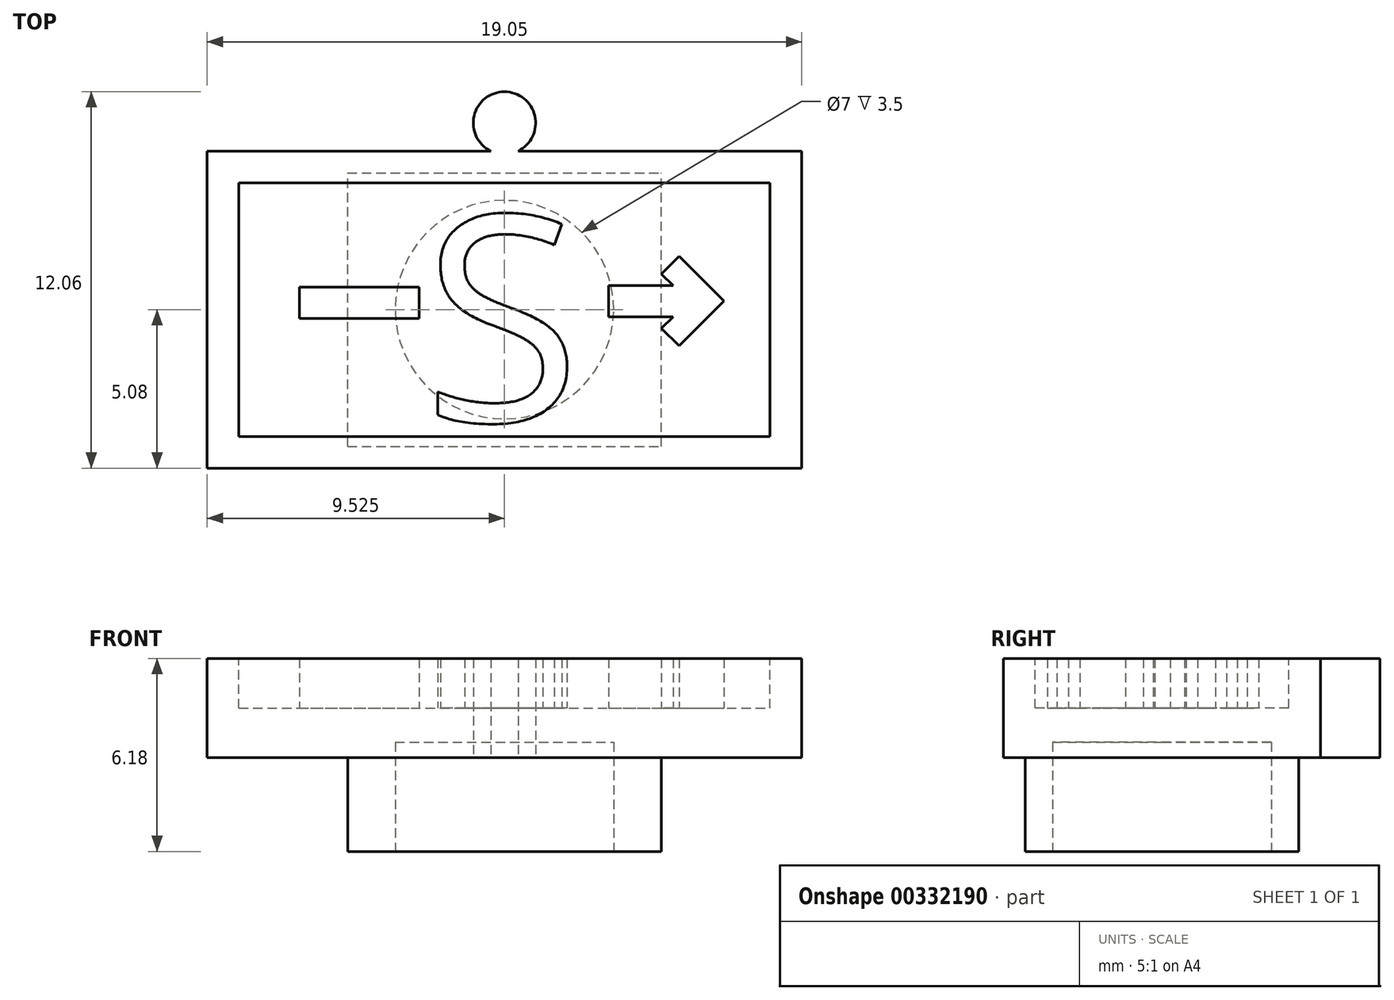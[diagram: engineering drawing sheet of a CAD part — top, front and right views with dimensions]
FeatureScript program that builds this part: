
annotation { "Feature Type Name" : "Feature", "Feature Type Description" : "" }
export const myFeature = defineFeature(function(context is Context, id is Id, definition is map)
    precondition{}
    {
        {
            var Q0;
            Q0=qCreatedBy(makeId("Top.planeOp"),FACE);
            var sketch = newSketch(context, id + "F0", { "sketchPlane" : qUnion([Q0])});
            skLineSegment(sketch, "E0.bottom", {"start": v(-19.05, 10.16) * mm, "end": v(0, 10.16) * mm});
            skLineSegment(sketch, "E0.top", {"start": v(-19.05, 0) * mm, "end": v(0, 0) * mm});
            skLineSegment(sketch, "E0.left", {"start": v(-19.05, 10.16) * mm, "end": v(-19.05, 0) * mm});
            skLineSegment(sketch, "E0.right", {"start": v(0, 10.16) * mm, "end": v(0, 0) * mm});
            skCircle(sketch, "E1", {"center": v(-9.53, 11.06) * mm, "radius": 1 * mm});
            skLineSegment(sketch, "E2", {"start": v(-9.52, 10.16) * mm, "end": v(-9.52, 0) * mm, "construction": true});
            skSolve(sketch);
        }
        {
            var Q0;
            Q0=qSketchRegion(id+"F0",true);
            extrude(context, id + "F1", {"entities" : qUnion([Q0]), "depth" : 3.17 * mm});
        }
        {
            var Q0;
            Q0=makeQuery(id+"F1.opExtrude","CAP_FACE",FACE,{"disambiguationData":[OSD([sQuery(id+"F0.wireOp",EDGE,"E0.bottom"),sQuery(id+"F0.wireOp",EDGE,"E0.top"),sQuery(id+"F0.wireOp",EDGE,"E0.left"),sQuery(id+"F0.wireOp",EDGE,"E0.right")])],"isStart":false});
            var sketch = newSketch(context, id + "F2", { "sketchPlane" : qUnion([Q0])});
            skLineSegment(sketch, "E3.bottom", {"start": v(-18.03, 9.14) * mm, "end": v(-1.02, 9.14) * mm});
            skLineSegment(sketch, "E3.top", {"start": v(-18.03, 1.02) * mm, "end": v(-1.02, 1.02) * mm});
            skLineSegment(sketch, "E3.left", {"start": v(-18.03, 9.14) * mm, "end": v(-18.03, 1.02) * mm});
            skLineSegment(sketch, "E3.right", {"start": v(-1.02, 9.14) * mm, "end": v(-1.02, 1.02) * mm});
            skSolve(sketch);
        }
        {
            var Q0;
            Q0=qSketchRegion(id+"F2",true);
            extrude(context, id + "F3", {"entities" : qUnion([Q0]), "operationType" : NewBodyOperationType.REMOVE, "oppositeDirection" : true, "depth" : 1.59 * mm});
        }
        {
            var Q0;
            Q0=makeQuery(id+"F1.opExtrude","CAP_FACE",FACE,{"disambiguationData":[OSD([sQuery(id+"F0.wireOp",EDGE,"E0.bottom"),sQuery(id+"F0.wireOp",EDGE,"E0.top"),sQuery(id+"F0.wireOp",EDGE,"E0.left"),sQuery(id+"F0.wireOp",EDGE,"E0.right"),sQuery(id+"F0.wireOp",EDGE,"E1"),sQuery(id+"F0.wireOp",EDGE,"25aa8db4-dd9b-41d2-b8c9-1594e9b75191"),sQuery(id+"F0.wireOp",EDGE,"40f63cb3-13d8-4821-a3c4-c05e674bd89b0.MirrorC")])],"isStart":true});
            var sketch = newSketch(context, id + "F4", { "sketchPlane" : qUnion([Q0])});
            skLineSegment(sketch, "E4.bottom", {"start": v(-14.55, -0.7) * mm, "end": v(-4.5, -0.7) * mm});
            skLineSegment(sketch, "E4.top", {"start": v(-14.55, -9.46) * mm, "end": v(-4.5, -9.46) * mm});
            skLineSegment(sketch, "E4.left", {"start": v(-14.55, -0.7) * mm, "end": v(-14.55, -9.46) * mm});
            skLineSegment(sketch, "E4.right", {"start": v(-4.5, -0.7) * mm, "end": v(-4.5, -9.46) * mm});
            skSolve(sketch);
        }
        {
            var Q0;
            Q0=qSketchRegion(id+"F4",true);
            extrude(context, id + "F5", {"entities" : qUnion([Q0]), "operationType" : NewBodyOperationType.ADD, "depth" : 3 * mm, "offsetDistance" : 25 * mm});
        }
        {
            var Q0;
            Q0=makeQuery(id+"F5.opExtrude","CAP_FACE",FACE,{"disambiguationData":[OSD([sQuery(id+"F4.wireOp",EDGE,"E4.bottom"),sQuery(id+"F4.wireOp",EDGE,"E4.top"),sQuery(id+"F4.wireOp",EDGE,"E4.left"),sQuery(id+"F4.wireOp",EDGE,"E4.right")])],"isStart":false});
            var sketch = newSketch(context, id + "F6", { "sketchPlane" : qUnion([Q0])});
            skCircle(sketch, "E5", {"center": v(-9.52, -5.08) * mm, "radius": 3.5 * mm});
            skLineSegment(sketch, "E6", {"start": v(-19.05, -5.08) * mm, "end": v(0, -5.08) * mm, "construction": true});
            skPoint(sketch, "E6.endSnap0", {"position": v(-4.5, -5.08) * mm});
            skLineSegment(sketch, "E7", {"start": v(-9.53, 0) * mm, "end": v(-9.53, -9.46) * mm, "construction": true});
            skSolve(sketch);
        }
        {
            var Q0;
            Q0=makeQuery(id+"F6.imprint","IMPRINT",FACE,{"disambiguationData":[TD([[makeQuery(id+"F6.imprint","IMPRINT",EDGE,{"derivedFrom":sQuery(id+"F6.wireOp",EDGE,"E5")}),1.0]])]});
            extrude(context, id + "F7", {"entities" : qUnion([Q0]), "operationType" : NewBodyOperationType.REMOVE, "oppositeDirection" : true, "depth" : 3.5 * mm, "offsetDistance" : 25 * mm});
        }
        {
            var Q0;
            Q0=makeQuery(id+"F3.boolean.opBoolean","COPY",FACE,{"derivedFrom":makeQuery(id+"F3.opExtrude","CAP_FACE",FACE,{"disambiguationData":[OSD([sQuery(id+"F2.wireOp",EDGE,"E3.bottom"),sQuery(id+"F2.wireOp",EDGE,"E3.top"),sQuery(id+"F2.wireOp",EDGE,"E3.left"),sQuery(id+"F2.wireOp",EDGE,"E3.right")])],"isStart":false})});
            var sketch = newSketch(context, id + "F8", { "sketchPlane" : qUnion([Q0])});
            skLineSegment(sketch, "E8", {"start": v(-9.53, 10.16) * mm, "end": v(-9.52, 0) * mm, "construction": true});
            skLineSegment(sketch, "E9.bottom", {"start": v(-16.1, 5.8) * mm, "end": v(-12.26, 5.8) * mm});
            skLineSegment(sketch, "E9.top", {"start": v(-16.1, 4.8) * mm, "end": v(-12.26, 4.8) * mm});
            skLineSegment(sketch, "E9.left", {"start": v(-16.1, 5.8) * mm, "end": v(-16.1, 4.8) * mm});
            skLineSegment(sketch, "E9.right", {"start": v(-12.26, 5.8) * mm, "end": v(-12.26, 4.8) * mm});
            skLineSegment(sketch, "E10", {"start": v(-6.19, 5.85) * mm, "end": v(-4.12, 5.85) * mm});
            skLineSegment(sketch, "E11", {"start": v(-4.12, 5.85) * mm, "end": v(-4.5, 6.22) * mm});
            skLineSegment(sketch, "E12", {"start": v(-4.5, 6.22) * mm, "end": v(-3.93, 6.79) * mm});
            skLineSegment(sketch, "E13", {"start": v(-3.93, 6.79) * mm, "end": v(-2.5, 5.35) * mm});
            skLineSegment(sketch, "E14", {"start": v(-2.5, 5.35) * mm, "end": v(-3.93, 3.92) * mm});
            skLineSegment(sketch, "E15", {"start": v(-3.93, 3.92) * mm, "end": v(-4.5, 4.48) * mm});
            skLineSegment(sketch, "E16", {"start": v(-4.5, 4.48) * mm, "end": v(-4.12, 4.85) * mm});
            skLineSegment(sketch, "E17", {"start": v(-4.12, 4.85) * mm, "end": v(-6.19, 4.85) * mm});
            skLineSegment(sketch, "E18", {"start": v(-6.19, 4.85) * mm, "end": v(-6.19, 5.85) * mm});
            skText(sketch, "E19", { "text": "S\n", "fontName": "OpenSans-Regular.ttf"});
            skPoint(sketch, "E19.firstSnap0", {"position": v(-9.52, 8.14) * mm});
            const initialGuessF8  = {"E19": [-0.01214, 0.0015, 1, 0, 0.00664]};
            skSetInitialGuess(sketch, initialGuessF8);
            skSolve(sketch);
        }
        {
            var Q0;
            Q0 = qSketchRegion(id + "F8", true);
            var Q1;
            Q1=makeQuery(id+"F1.opExtrude","CAP_FACE",FACE,{"disambiguationData":[OSD([sQuery(id+"F0.wireOp",EDGE,"E0.bottom"),sQuery(id+"F0.wireOp",EDGE,"E0.top"),sQuery(id+"F0.wireOp",EDGE,"E0.left"),sQuery(id+"F0.wireOp",EDGE,"E0.right"),sQuery(id+"F0.wireOp",EDGE,"E1"),sQuery(id+"F0.wireOp",EDGE,"25aa8db4-dd9b-41d2-b8c9-1594e9b75191"),sQuery(id+"F0.wireOp",EDGE,"40f63cb3-13d8-4821-a3c4-c05e674bd89b0.MirrorC")])],"isStart":false});
            extrude(context, id + "F9", {"entities" : qUnion([Q0]), "operationType" : NewBodyOperationType.ADD, "endBound" : BoundingType.UP_TO_SURFACE, "depth" : 25 * mm, "endBoundEntityFace" : qUnion([Q1]), "offsetDistance" : 25 * mm});
        }
    });
